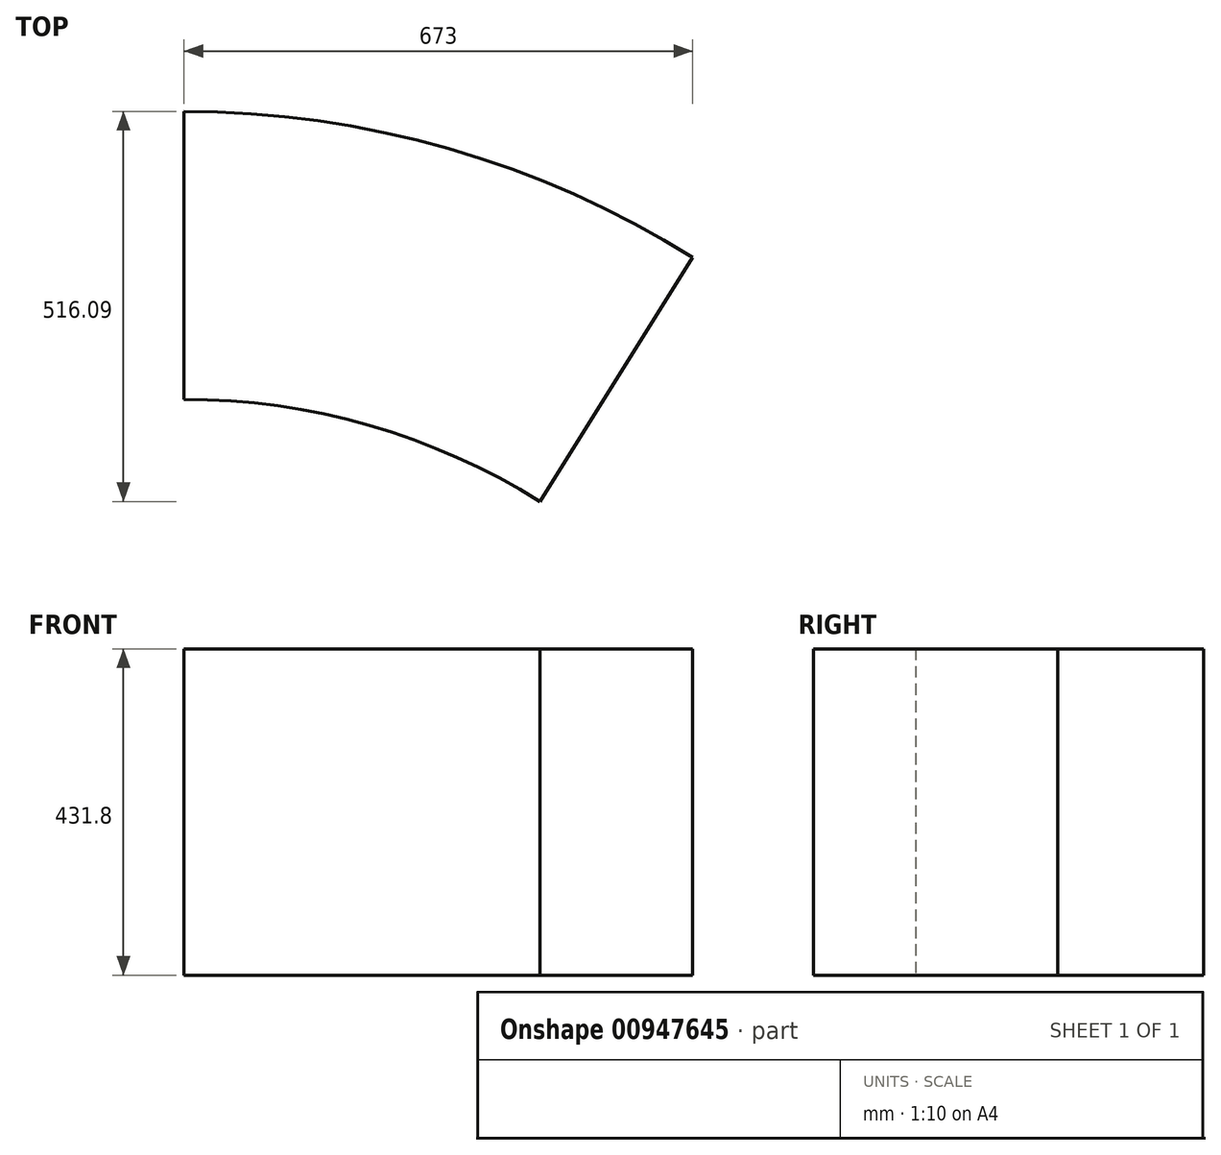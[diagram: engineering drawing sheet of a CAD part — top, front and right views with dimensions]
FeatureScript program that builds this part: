
annotation { "Feature Type Name" : "Feature", "Feature Type Description" : "" }
export const myFeature = defineFeature(function(context is Context, id is Id, definition is map)
    precondition{}
    {
        {
            var Q0;
            Q0=qCreatedBy(makeId("Top.planeOp"),FACE);
            var sketch = newSketch(context, id + "F0", { "sketchPlane" : qUnion([Q0])});
            skCircle(sketch, "E0", {"center": v(0, 0) * mm, "radius": 1270 * mm});
            skCircle(sketch, "E1", {"center": v(0, 0) * mm, "radius": 889 * mm});
            skSolve(sketch);
        }
        {
            var Q0;
            Q0=qCreatedBy(makeId("Top.planeOp"),FACE);
            var Q1;
            Q1=qCreatedBy(makeId("Top.planeOp"),FACE);
            var sketch = newSketch(context, id + "F1", { "sketchPlane" : qUnion([Q0, Q1])});
            skLineSegment(sketch, "E2", {"start": v(0, 889) * mm, "end": v(0, 1270) * mm});
            skLineSegment(sketch, "E3", {"start": v(471.1, 753.91) * mm, "end": v(674.7, 1079.76) * mm});
            skArc(sketch, "E4.0", {"start": v(673, 1077.02) * mm, "mid": v(350.06, 1220.8) * mm, "end": v(0, 1270) * mm});
            skArc(sketch, "E5.0", {"start": v(471.1, 753.91) * mm, "mid": v(245.04, 854.56) * mm, "end": v(0, 889) * mm});
            skSolve(sketch);
        }
        {
            var Q0;
            Q0 = qSketchRegion(id + "F1", true);
            extrude(context, id + "F2", {"entities" : qUnion([Q0]), "depth" : 431.8 * mm, "offsetDistance" : 25.4 * mm});
        }
    });
